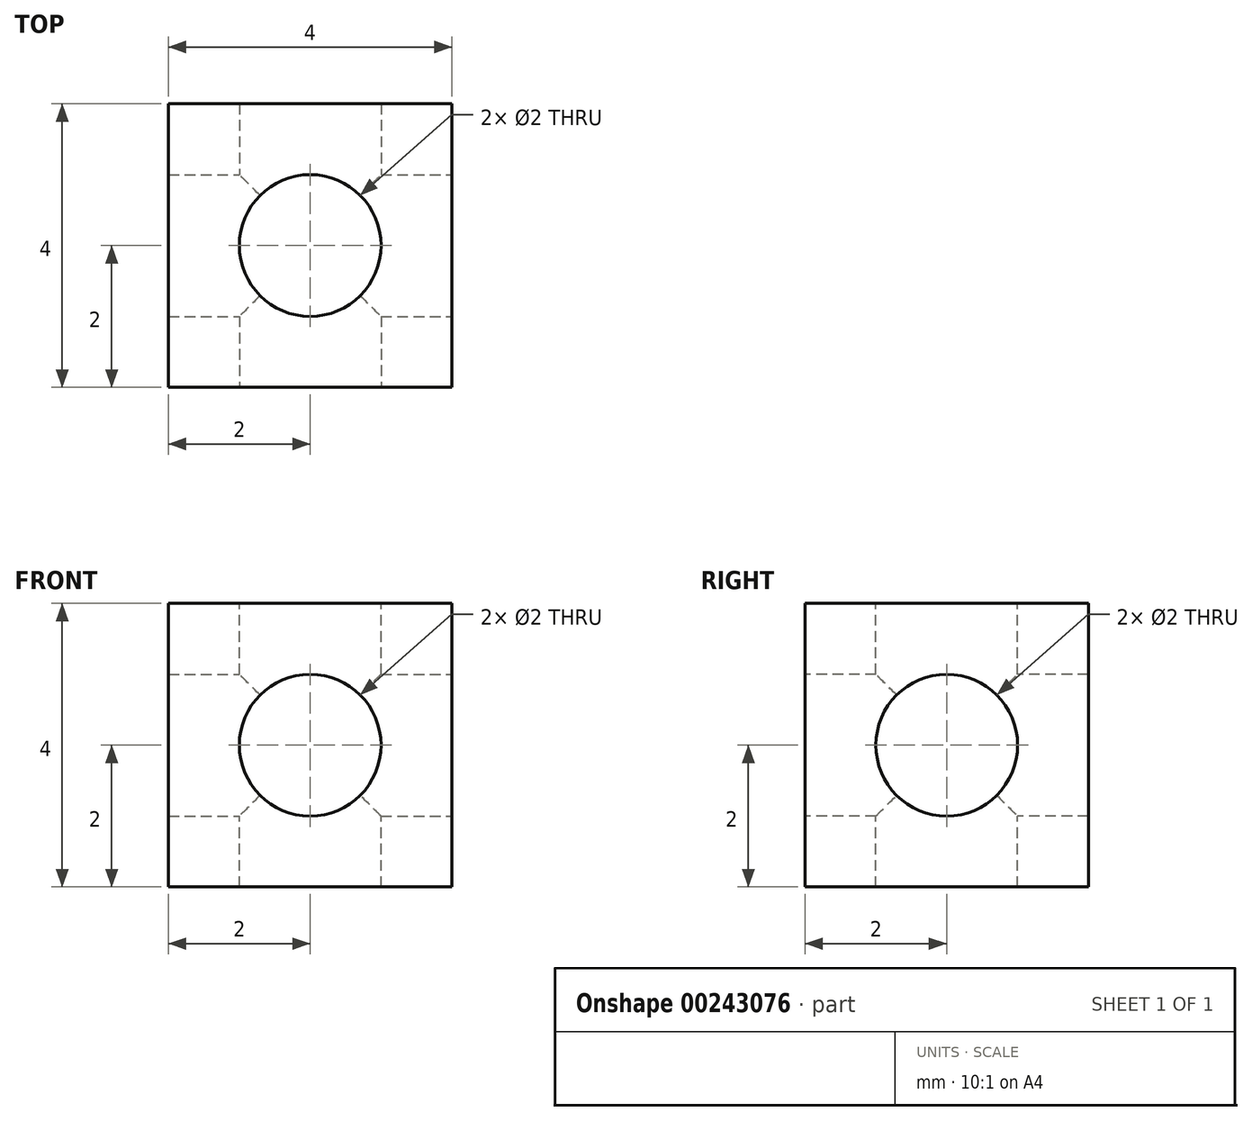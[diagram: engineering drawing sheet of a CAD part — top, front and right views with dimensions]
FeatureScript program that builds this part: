
annotation { "Feature Type Name" : "Feature", "Feature Type Description" : "" }
export const myFeature = defineFeature(function(context is Context, id is Id, definition is map)
    precondition{}
    {
        {
            var Q0;
            Q0=qCreatedBy(makeId("Top.planeOp"),FACE);
            var sketch = newSketch(context, id + "F0", { "sketchPlane" : qUnion([Q0])});
            skLineSegment(sketch, "E0.bottom", {"start": v(0, 0) * mm, "end": v(4, 0) * mm});
            skLineSegment(sketch, "E0.top", {"start": v(0, 4) * mm, "end": v(4, 4) * mm});
            skLineSegment(sketch, "E0.left", {"start": v(0, 0) * mm, "end": v(0, 4) * mm});
            skLineSegment(sketch, "E0.right", {"start": v(4, 0) * mm, "end": v(4, 4) * mm});
            skSolve(sketch);
        }
        {
            var Q0;
            Q0 = qSketchRegion(id + "F0", true);
            extrude(context, id + "F1", {"entities" : qUnion([Q0]), "depth" : 4 * mm});
        }
        {
            var Q0;
            Q0=makeQuery(id+"F1.opExtrude","SWEPT_FACE",FACE,{"disambiguationData":[OSD([sQuery(id+"F0.wireOp",EDGE,"E0.bottom")])]});
            var sketch = newSketch(context, id + "F2", { "sketchPlane" : qUnion([Q0])});
            skCircle(sketch, "E1", {"center": v(2, 2) * mm, "radius": 1 * mm});
            skPoint(sketch, "E1.centerSnap0", {"position": v(4, 2) * mm});
            skPoint(sketch, "E1.centerSnap1", {"position": v(2, 4) * mm});
            skSolve(sketch);
        }
        {
            var Q0;
            Q0 = qSketchRegion(id + "F2", true);
            extrude(context, id + "F3", {"entities" : qUnion([Q0]), "operationType" : NewBodyOperationType.REMOVE, "oppositeDirection" : true, "depth" : 25 * mm});
        }
        {
            var Q0;
            Q0=makeQuery(id+"F1.opExtrude","CAP_FACE",FACE,{"disambiguationData":[OSD([sQuery(id+"F0.wireOp",EDGE,"E0.bottom"),sQuery(id+"F0.wireOp",EDGE,"E0.top"),sQuery(id+"F0.wireOp",EDGE,"E0.left"),sQuery(id+"F0.wireOp",EDGE,"E0.right")])],"isStart":false});
            var sketch = newSketch(context, id + "F4", { "sketchPlane" : qUnion([Q0])});
            skCircle(sketch, "E2", {"center": v(2, 2) * mm, "radius": 1 * mm});
            skPoint(sketch, "E2.centerSnap0", {"position": v(4, 2) * mm});
            skPoint(sketch, "E2.centerSnap1", {"position": v(2, 4) * mm});
            skSolve(sketch);
        }
        {
            var Q0;
            Q0 = qSketchRegion(id + "F4", true);
            extrude(context, id + "F5", {"entities" : qUnion([Q0]), "operationType" : NewBodyOperationType.REMOVE, "oppositeDirection" : true, "depth" : 25 * mm});
        }
        {
            var Q0;
            Q0=makeQuery(id+"F1.opExtrude","SWEPT_FACE",FACE,{"disambiguationData":[OSD([sQuery(id+"F0.wireOp",EDGE,"E0.right")])]});
            var sketch = newSketch(context, id + "F6", { "sketchPlane" : qUnion([Q0])});
            skCircle(sketch, "E3", {"center": v(2, 2) * mm, "radius": 1 * mm});
            skPoint(sketch, "E3.centerSnap0", {"position": v(0, 2) * mm});
            skPoint(sketch, "E3.centerSnap1", {"position": v(2, 4) * mm});
            skSolve(sketch);
        }
        {
            var Q0;
            Q0 = qSketchRegion(id + "F6", true);
            extrude(context, id + "F7", {"entities" : qUnion([Q0]), "operationType" : NewBodyOperationType.REMOVE, "oppositeDirection" : true, "depth" : 25 * mm});
        }
    });
